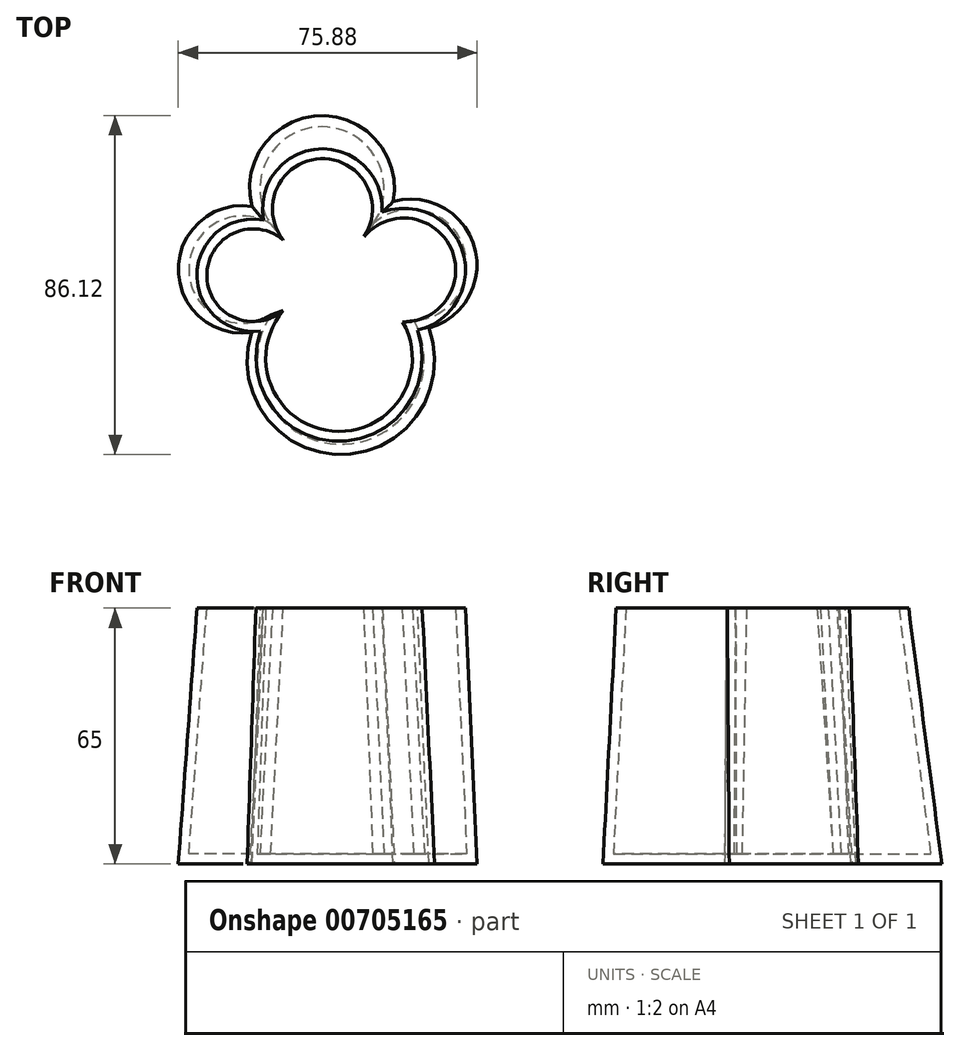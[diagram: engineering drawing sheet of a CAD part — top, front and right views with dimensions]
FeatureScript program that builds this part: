
annotation { "Feature Type Name" : "Feature", "Feature Type Description" : "" }
export const myFeature = defineFeature(function(context is Context, id is Id, definition is map)
    precondition{}
    {
        {
            var Q0;
            Q0=qCreatedBy(makeId("Top.planeOp"),FACE);
            var sketch = newSketch(context, id + "F0", { "sketchPlane" : qUnion([Q0])});
            skArc(sketch, "E0", {"start": v(-18.36, 11.7) * mm, "mid": v(-1.42, -21.1) * mm, "end": v(18.07, 10.26) * mm});
            skArc(sketch, "E1", {"start": v(-18.36, 34.83) * mm, "mid": v(-39.16, 23.27) * mm, "end": v(-18.36, 11.7) * mm});
            skArc(sketch, "E2", {"start": v(7.66, 34.83) * mm, "mid": v(-5.35, 59.53) * mm, "end": v(-18.36, 34.83) * mm});
            skArc(sketch, "E3", {"start": v(18.07, 10.26) * mm, "mid": v(30.3, 29.93) * mm, "end": v(7.66, 34.83) * mm});
            skSolve(sketch);
        }
        {
            var Q0;
            Q0=qCreatedBy(makeId("Top.planeOp"),FACE);
            cPlane(context, id + "F1", {"entities" : qUnion([Q0]), "cplaneType" : CPlaneType.OFFSET, "offset" : 62.5 * mm, "width" : 150 * mm, "height" : 150 * mm});
        }
        {
            var Q0;
            Q0=qCreatedBy(id+"F1.planeOp",FACE);
            var sketch = newSketch(context, id + "F2", { "sketchPlane" : qUnion([Q0])});
            skArc(sketch, "E4", {"start": v(5.35, 31.65) * mm, "mid": v(-5.77, 51.4) * mm, "end": v(-15.18, 30.79) * mm});
            skArc(sketch, "E5", {"start": v(-15.18, 30.79) * mm, "mid": v(-34.6, 21.82) * mm, "end": v(-15.18, 12.86) * mm});
            skArc(sketch, "E6", {"start": v(-15.18, 12.86) * mm, "mid": v(-2.78, -17.79) * mm, "end": v(15.18, 9.97) * mm});
            skArc(sketch, "E7", {"start": v(15.18, 9.97) * mm, "mid": v(27.46, 28.6) * mm, "end": v(5.35, 31.65) * mm});
            skSolve(sketch);
        }
        {
            var Q0;
            Q0=makeQuery(id+"F0.imprint","IMPRINT",FACE,{"disambiguationData":[TD([[makeQuery(id+"F0.imprint","IMPRINT",EDGE,{"derivedFrom":sQuery(id+"F0.wireOp",EDGE,"E0")}),1.0]])]});
            var Q1;
            Q1=makeQuery(id+"F2.imprint","IMPRINT",FACE,{"disambiguationData":[TD([[makeQuery(id+"F2.imprint","IMPRINT",EDGE,{"derivedFrom":sQuery(id+"F2.wireOp",EDGE,"E4")}),1.0]])]});
            loft(context, id + "F3", {"sheetProfilesArray" : [{ "sheetProfileEntities" : qUnion([Q0]) }, { "sheetProfileEntities" : qUnion([Q1]) }]});
        }
        {
            var Q0;
            Q0=makeQuery(id+"F3.opLoft","CAP_FACE",FACE,{"disambiguationData":[OSD([makeQuery(id+"F2.imprint","IMPRINT",FACE,{"disambiguationData":[TD([[makeQuery(id+"F2.imprint","IMPRINT",EDGE,{"derivedFrom":sQuery(id+"F2.wireOp",EDGE,"E4")}),1.0]])]})])],"isStart":true});
            shell(context, id + "F4", {"entities" : qUnion([Q0]), "thickness" : 2.5 * mm, "oppositeDirection" : true});
        }
    });
